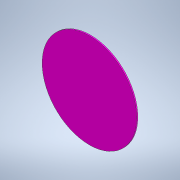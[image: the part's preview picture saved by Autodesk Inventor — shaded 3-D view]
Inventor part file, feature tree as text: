
AUTODESK INVENTOR PART (.ipt)
format: ipt  version: 2020.4 (Build 244396000, 396)  size: 93,696 bytes
history: native  units: mm
features: extrude x1, sketch x1
ambient origin geometry x8: Origin, YZ Plane, XZ Plane, XY Plane, X Axis, Y Axis, Z Axis, Center Point
bodies: Solid1 (feature_tree)
feature tree (2):
  extrude  "Extrusion1"  Depth=0.5mm TaperAngle=0.0deg
  sketch  "Sketch1"  dims[d0=42.0mm d1=0.5mm d2=0.0mm]
